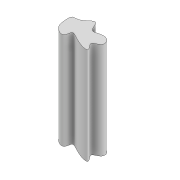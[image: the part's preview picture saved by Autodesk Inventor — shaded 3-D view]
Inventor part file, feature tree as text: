
AUTODESK INVENTOR PART (.ipt)
format: ipt  version: 2021 (Build 250183000, 183)  size: 120,320 bytes
history: native  units: in
note: dims shown in document units (in); Inventor stores cm internally (conversion verified against a paired STEP export)
features: extrude x1, sketch x1
ambient origin geometry x8: Origin, YZ Plane, XZ Plane, XY Plane, X Axis, Y Axis, Z Axis, Center Point
bodies: Body1 (feature_tree)
feature tree (2):
  extrude  "Extrusion2"  Depth=6.2992in TaperAngle=360.0deg
  sketch  "Sketch1"  dims[d0=118.1102in d1=6.2992in d3=360.0deg d7=1968.5039in d8=1.5748in d10=360.0deg d12=3.0in d13=5.0in d14=118.1102in d15=0.0in]
